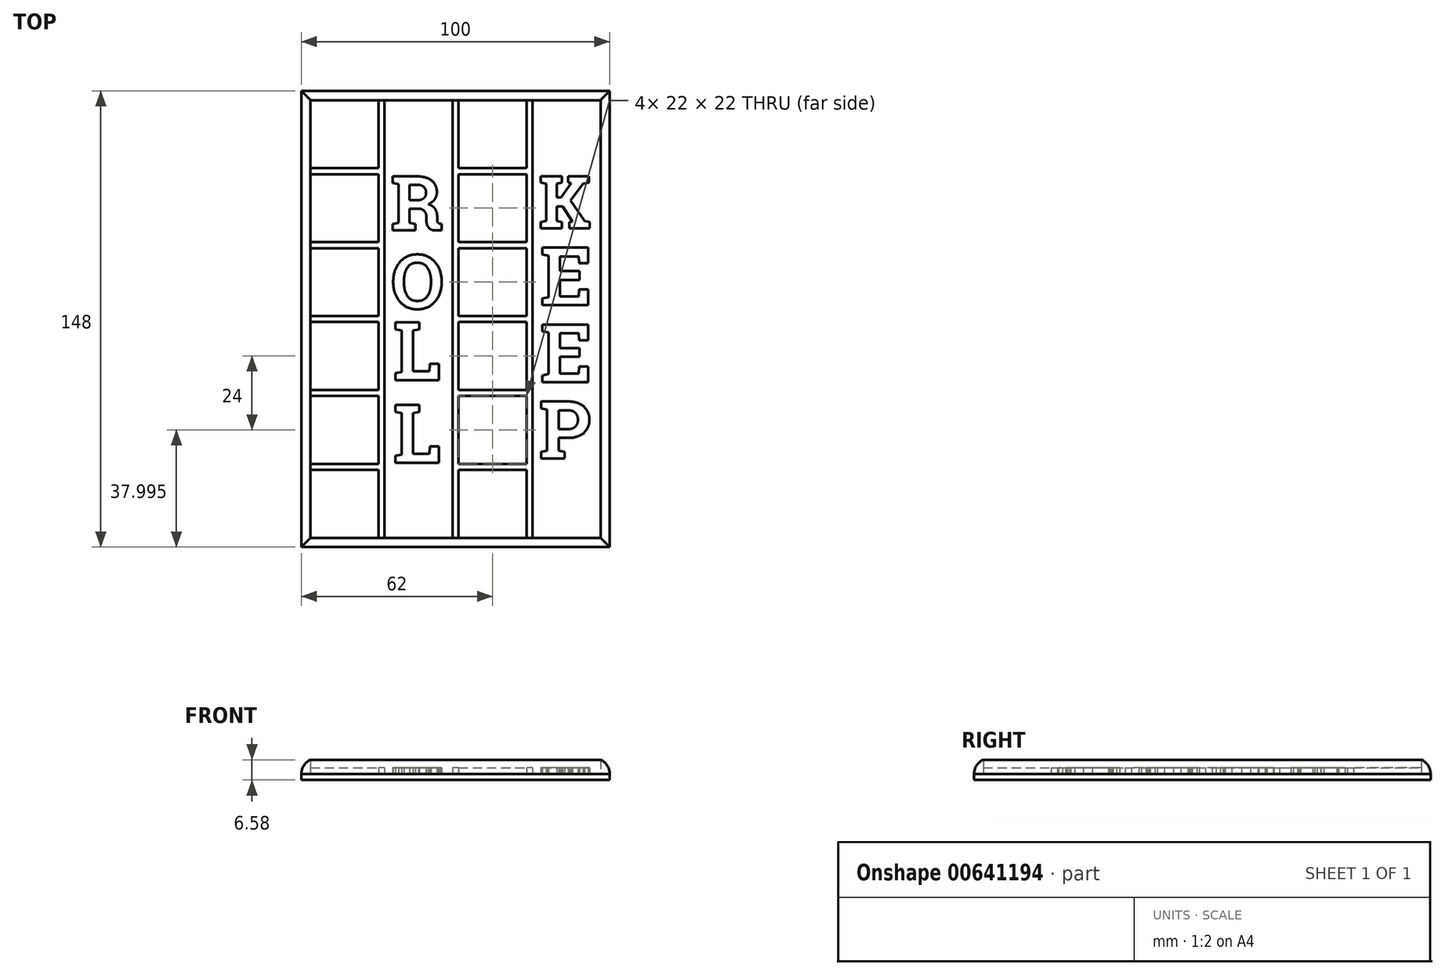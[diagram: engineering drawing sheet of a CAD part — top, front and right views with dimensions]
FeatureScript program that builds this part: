
annotation { "Feature Type Name" : "Feature", "Feature Type Description" : "" }
export const myFeature = defineFeature(function(context is Context, id is Id, definition is map)
    precondition{}
    {
        {
            var Q0;
            Q0=qCreatedBy(makeId("Top.planeOp"),FACE);
            var sketch = newSketch(context, id + "F0", { "sketchPlane" : qUnion([Q0])});
            skLineSegment(sketch, "E0.bottom", {"start": v(-50, 75.1) * mm, "end": v(50, 75.1) * mm});
            skLineSegment(sketch, "E0.top", {"start": v(-50, -72.9) * mm, "end": v(50, -72.9) * mm});
            skLineSegment(sketch, "E0.left", {"start": v(-50, 75.1) * mm, "end": v(-50, -72.9) * mm});
            skLineSegment(sketch, "E0.right", {"start": v(50, 75.1) * mm, "end": v(50, -72.9) * mm});
            skLineSegment(sketch, "E1.bottom", {"start": v(47, -69.9) * mm, "end": v(-47, -69.9) * mm});
            skLineSegment(sketch, "E1.top", {"start": v(47, 72.1) * mm, "end": v(-47, 72.1) * mm});
            skLineSegment(sketch, "E1.left", {"start": v(47, -69.9) * mm, "end": v(47, 72.1) * mm});
            skLineSegment(sketch, "E1.right", {"start": v(-47, -69.9) * mm, "end": v(-47, 72.1) * mm});
            skLineSegment(sketch, "E2", {"start": v(-25, 72.1) * mm, "end": v(-25, -69.9) * mm});
            skLineSegment(sketch, "E3.1.0.0", {"start": v(-1, 72.1) * mm, "end": v(-1, -69.9) * mm});
            skLineSegment(sketch, "E3.2.0.0", {"start": v(23, 72.1) * mm, "end": v(23, -69.9) * mm});
            skLineSegment(sketch, "E3.direction1", {"start": v(-25, -69.9) * mm, "end": v(-1, -69.9) * mm, "construction": true});
            skLineSegment(sketch, "E4", {"start": v(-23, -69.9) * mm, "end": v(-23, 72.1) * mm});
            skLineSegment(sketch, "E5.1.0.0", {"start": v(1, -69.9) * mm, "end": v(1, 72.1) * mm});
            skLineSegment(sketch, "E5.2.0.0", {"start": v(25, -69.9) * mm, "end": v(25, 72.1) * mm});
            skLineSegment(sketch, "E5.direction1", {"start": v(-23, -69.9) * mm, "end": v(1, -69.9) * mm, "construction": true});
            skSolve(sketch);
        }
        {
            var Q0;
            Q0=qCreatedBy(makeId("Top.planeOp"),FACE);
            var sketch = newSketch(context, id + "F1", { "sketchPlane" : qUnion([Q0])});
            skLineSegment(sketch, "E6", {"start": v(-47, -47.9) * mm, "end": v(47, -47.9) * mm});
            skLineSegment(sketch, "E7", {"start": v(-25, 72.1) * mm, "end": v(-25, -69.9) * mm});
            skLineSegment(sketch, "E8", {"start": v(-18.05, 72.1) * mm, "end": v(-40.05, 72.1) * mm});
            skLineSegment(sketch, "E9", {"start": v(-47, -69.9) * mm, "end": v(-47, 72.1) * mm});
            skLineSegment(sketch, "E10", {"start": v(-18.05, -69.9) * mm, "end": v(-40.05, -69.9) * mm});
            skLineSegment(sketch, "E11", {"start": v(1, -69.9) * mm, "end": v(1, 72.1) * mm});
            skLineSegment(sketch, "E12", {"start": v(29.95, -69.9) * mm, "end": v(7.95, -69.9) * mm});
            skLineSegment(sketch, "E13", {"start": v(23, 72.1) * mm, "end": v(23, -69.9) * mm});
            skLineSegment(sketch, "E14", {"start": v(29.95, 72.1) * mm, "end": v(7.95, 72.1) * mm});
            skLineSegment(sketch, "E15", {"start": v(-47, -23.9) * mm, "end": v(47, -23.9) * mm});
            skLineSegment(sketch, "E16", {"start": v(-47, -45.9) * mm, "end": v(47, -45.9) * mm});
            skLineSegment(sketch, "E17", {"start": v(-47, -21.9) * mm, "end": v(47, -21.9) * mm});
            skLineSegment(sketch, "E18", {"start": v(-47, 0.1) * mm, "end": v(47, 0.1) * mm});
            skLineSegment(sketch, "E19", {"start": v(-47, 2.1) * mm, "end": v(47, 2.1) * mm});
            skLineSegment(sketch, "E20", {"start": v(-47, 24.1) * mm, "end": v(47, 24.1) * mm});
            skLineSegment(sketch, "E21", {"start": v(-47, 26.1) * mm, "end": v(47, 26.1) * mm});
            skLineSegment(sketch, "E22", {"start": v(-47, 48.1) * mm, "end": v(47, 48.1) * mm});
            skLineSegment(sketch, "E23", {"start": v(-47, 50.1) * mm, "end": v(47, 50.1) * mm});
            skSolve(sketch);
        }
        {
            var Q0;
            Q0=makeQuery(id+"F0.imprint","IMPRINT",FACE,{"disambiguationData":[TD([[makeQuery(id+"F0.imprint","IMPRINT",EDGE,{"derivedFrom":sQuery(id+"F0.wireOp",EDGE,"E0.bottom")}),-1.0]])]});
            var Q1;
            Q1=sQuery(id+"F0.wireOp",EDGE,"E1.top");
            var Q2;
            Q2=sQuery(id+"F1.wireOp",EDGE,"E10");
            var Q3;
            Q3=sQuery(id+"F0.wireOp",EDGE,"E0.bottom");
            var Q4;
            Q4=sQuery(id+"F0.wireOp",EDGE,"E1.right");
            var Q5;
            Q5=sQuery(id+"F0.wireOp",EDGE,"E0.left");
            var Q6;
            Q6=sQuery(id+"F0.wireOp",EDGE,"E0.top");
            var Q7;
            Q7=sQuery(id+"F0.wireOp",EDGE,"E1.bottom");
            var Q8;
            Q8=sQuery(id+"F1.wireOp",EDGE,"E8");
            var Q9;
            Q9=sQuery(id+"F0.wireOp",EDGE,"E1.left");
            var Q10;
            Q10=sQuery(id+"F0.wireOp",EDGE,"E0.right");
            extrude(context, id + "F2", {"entities" : qUnion([Q0]), "surfaceEntities" : qUnion([Q1, Q2, Q3, Q4, Q5, Q6, Q7, Q8, Q9, Q10]), "depth" : 5 * mm, "offsetDistance" : 25 * mm});
        }
        {
            var Q0;
            {var subQ0=sQuery(id+"F0.wireOp",EDGE,"E2");Q0=makeQuery(id+"F0.imprint","IMPRINT",FACE,{"disambiguationData":[TD([[makeQuery(id+"F0.imprint","IMPRINT",EDGE,{"derivedFrom":subQ0}),1.0]])]});}
            var Q1;
            {var subQ0=sQuery(id+"F0.wireOp",EDGE,"E3.1.0.0");Q1=makeQuery(id+"F0.imprint","IMPRINT",FACE,{"disambiguationData":[TD([[makeQuery(id+"F0.imprint","IMPRINT",EDGE,{"derivedFrom":subQ0}),1.0]])]});}
            var Q2;
            {var subQ0=sQuery(id+"F0.wireOp",EDGE,"E3.2.0.0");Q2=makeQuery(id+"F0.imprint","IMPRINT",FACE,{"disambiguationData":[TD([[makeQuery(id+"F0.imprint","IMPRINT",EDGE,{"derivedFrom":subQ0}),1.0]])]});}
            var Q3;
            Q3=sQuery(id+"F0.wireOp",EDGE,"E2");
            var Q4;
            Q4=sQuery(id+"F0.wireOp",EDGE,"E4");
            extrude(context, id + "F3", {"entities" : qUnion([Q0, Q1, Q2]), "operationType" : NewBodyOperationType.ADD, "surfaceEntities" : qUnion([Q3, Q4]), "depth" : 2 * mm, "offsetDistance" : 25 * mm});
        }
        {
            var Q0;
            {var subQ0=sQuery(id+"F1.wireOp",EDGE,"E9");var subQ1=sQuery(id+"F1.wireOp",EDGE,"E6");var subQ2=makeQuery(id+"F1.imprint","INTERSECT",VERTEX,{"derivedFrom":[subQ1,subQ0]});Q0=makeQuery(id+"F1.imprint","IMPRINT",FACE,{"disambiguationData":[TD([[makeQuery(id+"F1.imprint","IMPRINT",EDGE,{"disambiguationData":[TD([[subQ2,-1.0]])],"derivedFrom":subQ1}),1.0]])]});}
            var Q1;
            {var subQ0=sQuery(id+"F1.wireOp",EDGE,"E13");var subQ1=sQuery(id+"F1.wireOp",EDGE,"E6");var subQ2=makeQuery(id+"F1.imprint","INTERSECT",VERTEX,{"derivedFrom":[subQ1,subQ0]});Q1=makeQuery(id+"F1.imprint","IMPRINT",FACE,{"disambiguationData":[TD([[makeQuery(id+"F1.imprint","IMPRINT",EDGE,{"disambiguationData":[TD([[subQ2,1.0]])],"derivedFrom":subQ1}),1.0]])]});}
            var Q2;
            {var subQ0=sQuery(id+"F1.wireOp",EDGE,"E15");var subQ1=sQuery(id+"F1.wireOp",EDGE,"E11");var subQ2=makeQuery(id+"F1.imprint","INTERSECT",VERTEX,{"derivedFrom":[subQ1,subQ0]});Q2=makeQuery(id+"F1.imprint","IMPRINT",FACE,{"disambiguationData":[TD([[makeQuery(id+"F1.imprint","IMPRINT",EDGE,{"disambiguationData":[TD([[subQ2,-1.0]])],"derivedFrom":subQ1}),-1.0]])]});}
            var Q3;
            {var subQ0=sQuery(id+"F1.wireOp",EDGE,"E18");var subQ1=sQuery(id+"F1.wireOp",EDGE,"E11");var subQ2=makeQuery(id+"F1.imprint","INTERSECT",VERTEX,{"derivedFrom":[subQ1,subQ0]});Q3=makeQuery(id+"F1.imprint","IMPRINT",FACE,{"disambiguationData":[TD([[makeQuery(id+"F1.imprint","IMPRINT",EDGE,{"disambiguationData":[TD([[subQ2,-1.0]])],"derivedFrom":subQ1}),-1.0]])]});}
            var Q4;
            {var subQ0=sQuery(id+"F1.wireOp",EDGE,"E17");var subQ1=sQuery(id+"F1.wireOp",EDGE,"E7");var subQ2=makeQuery(id+"F1.imprint","INTERSECT",VERTEX,{"derivedFrom":[subQ1,subQ0]});Q4=makeQuery(id+"F1.imprint","IMPRINT",FACE,{"disambiguationData":[TD([[makeQuery(id+"F1.imprint","IMPRINT",EDGE,{"disambiguationData":[TD([[subQ2,-1.0]])],"derivedFrom":subQ1}),-1.0]])]});}
            var Q5;
            {var subQ0=sQuery(id+"F1.wireOp",EDGE,"E19");var subQ1=sQuery(id+"F1.wireOp",EDGE,"E7");var subQ2=makeQuery(id+"F1.imprint","INTERSECT",VERTEX,{"derivedFrom":[subQ1,subQ0]});Q5=makeQuery(id+"F1.imprint","IMPRINT",FACE,{"disambiguationData":[TD([[makeQuery(id+"F1.imprint","IMPRINT",EDGE,{"disambiguationData":[TD([[subQ2,-1.0]])],"derivedFrom":subQ1}),-1.0]])]});}
            var Q6;
            {var subQ0=sQuery(id+"F1.wireOp",EDGE,"E21");var subQ1=sQuery(id+"F1.wireOp",EDGE,"E7");var subQ2=makeQuery(id+"F1.imprint","INTERSECT",VERTEX,{"derivedFrom":[subQ1,subQ0]});Q6=makeQuery(id+"F1.imprint","IMPRINT",FACE,{"disambiguationData":[TD([[makeQuery(id+"F1.imprint","IMPRINT",EDGE,{"disambiguationData":[TD([[subQ2,-1.0]])],"derivedFrom":subQ1}),-1.0]])]});}
            var Q7;
            {var subQ0=sQuery(id+"F1.wireOp",EDGE,"E23");var subQ1=sQuery(id+"F1.wireOp",EDGE,"E7");var subQ2=makeQuery(id+"F1.imprint","INTERSECT",VERTEX,{"derivedFrom":[subQ1,subQ0]});Q7=makeQuery(id+"F1.imprint","IMPRINT",FACE,{"disambiguationData":[TD([[makeQuery(id+"F1.imprint","IMPRINT",EDGE,{"disambiguationData":[TD([[subQ2,-1.0]])],"derivedFrom":subQ1}),-1.0]])]});}
            var Q8;
            {var subQ0=sQuery(id+"F1.wireOp",EDGE,"E23");var subQ1=sQuery(id+"F1.wireOp",EDGE,"E11");var subQ2=makeQuery(id+"F1.imprint","INTERSECT",VERTEX,{"derivedFrom":[subQ1,subQ0]});Q8=makeQuery(id+"F1.imprint","IMPRINT",FACE,{"disambiguationData":[TD([[makeQuery(id+"F1.imprint","IMPRINT",EDGE,{"disambiguationData":[TD([[subQ2,1.0]])],"derivedFrom":subQ1}),-1.0]])]});}
            var Q9;
            {var subQ0=sQuery(id+"F1.wireOp",EDGE,"E20");var subQ1=sQuery(id+"F1.wireOp",EDGE,"E11");var subQ2=makeQuery(id+"F1.imprint","INTERSECT",VERTEX,{"derivedFrom":[subQ1,subQ0]});Q9=makeQuery(id+"F1.imprint","IMPRINT",FACE,{"disambiguationData":[TD([[makeQuery(id+"F1.imprint","IMPRINT",EDGE,{"disambiguationData":[TD([[subQ2,-1.0]])],"derivedFrom":subQ1}),-1.0]])]});}
            extrude(context, id + "F4", {"entities" : qUnion([Q0, Q1, Q2, Q3, Q4, Q5, Q6, Q7, Q8, Q9]), "operationType" : NewBodyOperationType.ADD, "depth" : 2 * mm, "offsetDistance" : 25 * mm});
        }
        {
            var Q0;
            Q0=makeQuery(id+"F2.opExtrude","CAP_EDGE",EDGE,{"disambiguationData":[OSD([sQuery(id+"F0.wireOp",EDGE,"E0.right")])],"isStart":false});
            var Q1;
            Q1=makeQuery(id+"F2.opExtrude","CAP_EDGE",EDGE,{"disambiguationData":[OSD([sQuery(id+"F0.wireOp",EDGE,"E0.top")])],"isStart":false});
            var Q2;
            Q2=makeQuery(id+"F2.opExtrude","CAP_EDGE",EDGE,{"disambiguationData":[OSD([sQuery(id+"F0.wireOp",EDGE,"E0.left")])],"isStart":false});
            var Q3;
            Q3=makeQuery(id+"F2.opExtrude","CAP_EDGE",EDGE,{"disambiguationData":[OSD([sQuery(id+"F0.wireOp",EDGE,"E0.bottom")])],"isStart":false});
            fillet(context, id + "F5", {"entities" : qUnion([Q0, Q1, Q2, Q3]), "radius" : 5 * mm, "tangentPropagation" : true, "allowEdgeOverflow" : false});
        }
        {
            var Q0;
            Q0=qCreatedBy(makeId("Top.planeOp"),FACE);
            var sketch = newSketch(context, id + "F6", { "sketchPlane" : qUnion([Q0])});
            skLineSegment(sketch, "E24.bottom", {"start": v(-50, -72.9) * mm, "end": v(50, -72.9) * mm});
            skLineSegment(sketch, "E24.top", {"start": v(-50, 75.1) * mm, "end": v(50, 75.1) * mm});
            skLineSegment(sketch, "E24.left", {"start": v(-50, -72.9) * mm, "end": v(-50, 75.1) * mm});
            skLineSegment(sketch, "E24.right", {"start": v(50, -72.9) * mm, "end": v(50, 75.1) * mm});
            skSolve(sketch);
        }
        {
            var Q0;
            Q0 = qSketchRegion(id + "F6", true);
            extrude(context, id + "F7", {"entities" : qUnion([Q0]), "oppositeDirection" : true, "depth" : 2 * mm, "offsetDistance" : 25 * mm});
        }
        {
            var Q0;
            Q0=qCreatedBy(makeId("Top.planeOp"),FACE);
            var sketch = newSketch(context, id + "F8", { "sketchPlane" : qUnion([Q0])});
            skText(sketch, "E25", { "text": "R", "fontName": "RobotoSlab-Bold.ttf"});
            const initialGuessF8  = {"E25": [-0.021, 0.02983, 1, 0, 0.01777]};
            skSetInitialGuess(sketch, initialGuessF8);
            skSolve(sketch);
        }
        {
            var Q0;
            Q0=qCreatedBy(makeId("Top.planeOp"),FACE);
            var sketch = newSketch(context, id + "F9", { "sketchPlane" : qUnion([Q0])});
            skText(sketch, "E26", { "text": "O", "fontName": "RobotoSlab-Bold.ttf"});
            const initialGuessF9  = {"E26": [-0.021, 0.0045, 1, 0, 0.01755], "E26": [-0.021, 0.0045, 1, 0, 0.01755]};
            skSetInitialGuess(sketch, initialGuessF9);
            skSolve(sketch);
        }
        {
            var Q0;
            Q0 = qSketchRegion(id + "F8", true);
            extrude(context, id + "F10", {"entities" : qUnion([Q0]), "operationType" : NewBodyOperationType.ADD, "depth" : 2 * mm, "offsetDistance" : 25 * mm});
        }
        {
            var Q0;
            Q0 = qSketchRegion(id + "F9", true);
            extrude(context, id + "F11", {"entities" : qUnion([Q0]), "operationType" : NewBodyOperationType.ADD, "depth" : 2 * mm, "offsetDistance" : 25 * mm});
        }
        {
            var Q0;
            Q0=qCreatedBy(makeId("Top.planeOp"),FACE);
            var sketch = newSketch(context, id + "F12", { "sketchPlane" : qUnion([Q0])});
            skText(sketch, "E27", { "text": "L", "fontName": "RobotoSlab-Bold.ttf"});
            const initialGuessF12  = {"E27": [-0.02022, -0.01872, 1, 0, 0.019]};
            skSetInitialGuess(sketch, initialGuessF12);
            skSolve(sketch);
        }
        {
            var Q0;
            Q0=qCreatedBy(makeId("Top.planeOp"),FACE);
            var sketch = newSketch(context, id + "F13", { "sketchPlane" : qUnion([Q0])});
            skText(sketch, "E28", { "text": "L", "fontName": "RobotoSlab-Bold.ttf"});
            const initialGuessF13  = {"E28": [-0.02022, -0.0455, 1, 0, 0.019]};
            skSetInitialGuess(sketch, initialGuessF13);
            skSolve(sketch);
        }
        {
            var Q0;
            Q0 = qSketchRegion(id + "F12", true);
            extrude(context, id + "F14", {"entities" : qUnion([Q0]), "operationType" : NewBodyOperationType.ADD, "depth" : 2 * mm, "offsetDistance" : 25 * mm});
        }
        {
            var Q0;
            Q0 = qSketchRegion(id + "F13", true);
            extrude(context, id + "F15", {"entities" : qUnion([Q0]), "operationType" : NewBodyOperationType.ADD, "depth" : 2 * mm, "offsetDistance" : 25 * mm});
        }
        {
            var Q0;
            Q0=qCreatedBy(makeId("Top.planeOp"),FACE);
            var sketch = newSketch(context, id + "F16", { "sketchPlane" : qUnion([Q0])});
            skText(sketch, "E29", { "text": "K", "fontName": "RobotoSlab-Bold.ttf"});
            const initialGuessF16  = {"E29": [0.027, 0.03057, 1, 0, 0.01703]};
            skSetInitialGuess(sketch, initialGuessF16);
            skSolve(sketch);
        }
        {
            var Q0;
            Q0=qCreatedBy(makeId("Top.planeOp"),FACE);
            var sketch = newSketch(context, id + "F17", { "sketchPlane" : qUnion([Q0])});
            skText(sketch, "E30", { "text": "E", "fontName": "RobotoSlab-Bold.ttf"});
            const initialGuessF17  = {"E30": [0.0274, 0.00557, 1, 0, 0.019]};
            skSetInitialGuess(sketch, initialGuessF17);
            skSolve(sketch);
        }
        {
            var Q0;
            Q0=qCreatedBy(makeId("Top.planeOp"),FACE);
            var sketch = newSketch(context, id + "F18", { "sketchPlane" : qUnion([Q0])});
            skText(sketch, "E31", { "text": "E", "fontName": "RobotoSlab-Bold.ttf"});
            const initialGuessF18  = {"E31": [0.0274, -0.01943, 1, 0, 0.019]};
            skSetInitialGuess(sketch, initialGuessF18);
            skSolve(sketch);
        }
        {
            var Q0;
            Q0=qCreatedBy(makeId("Top.planeOp"),FACE);
            var sketch = newSketch(context, id + "F19", { "sketchPlane" : qUnion([Q0])});
            skText(sketch, "E32", { "text": "P", "fontName": "RobotoSlab-Bold.ttf"});
            const initialGuessF19  = {"E32": [0.027, -0.0442, 1, 0, 0.01878]};
            skSetInitialGuess(sketch, initialGuessF19);
            skSolve(sketch);
        }
        {
            var Q0;
            Q0 = qSketchRegion(id + "F17", true);
            extrude(context, id + "F20", {"entities" : qUnion([Q0]), "operationType" : NewBodyOperationType.ADD, "depth" : 2 * mm, "offsetDistance" : 25 * mm});
        }
        {
            var Q0;
            Q0 = qSketchRegion(id + "F18", true);
            extrude(context, id + "F21", {"entities" : qUnion([Q0]), "operationType" : NewBodyOperationType.ADD, "depth" : 2 * mm, "offsetDistance" : 25 * mm});
        }
        {
            var Q0;
            Q0 = qSketchRegion(id + "F19", true);
            extrude(context, id + "F22", {"entities" : qUnion([Q0]), "operationType" : NewBodyOperationType.ADD, "depth" : 2 * mm, "offsetDistance" : 25 * mm});
        }
        {
            var Q0;
            Q0 = qSketchRegion(id + "F16", true);
            extrude(context, id + "F23", {"entities" : qUnion([Q0]), "operationType" : NewBodyOperationType.ADD, "depth" : 2 * mm, "offsetDistance" : 25 * mm});
        }
    });
